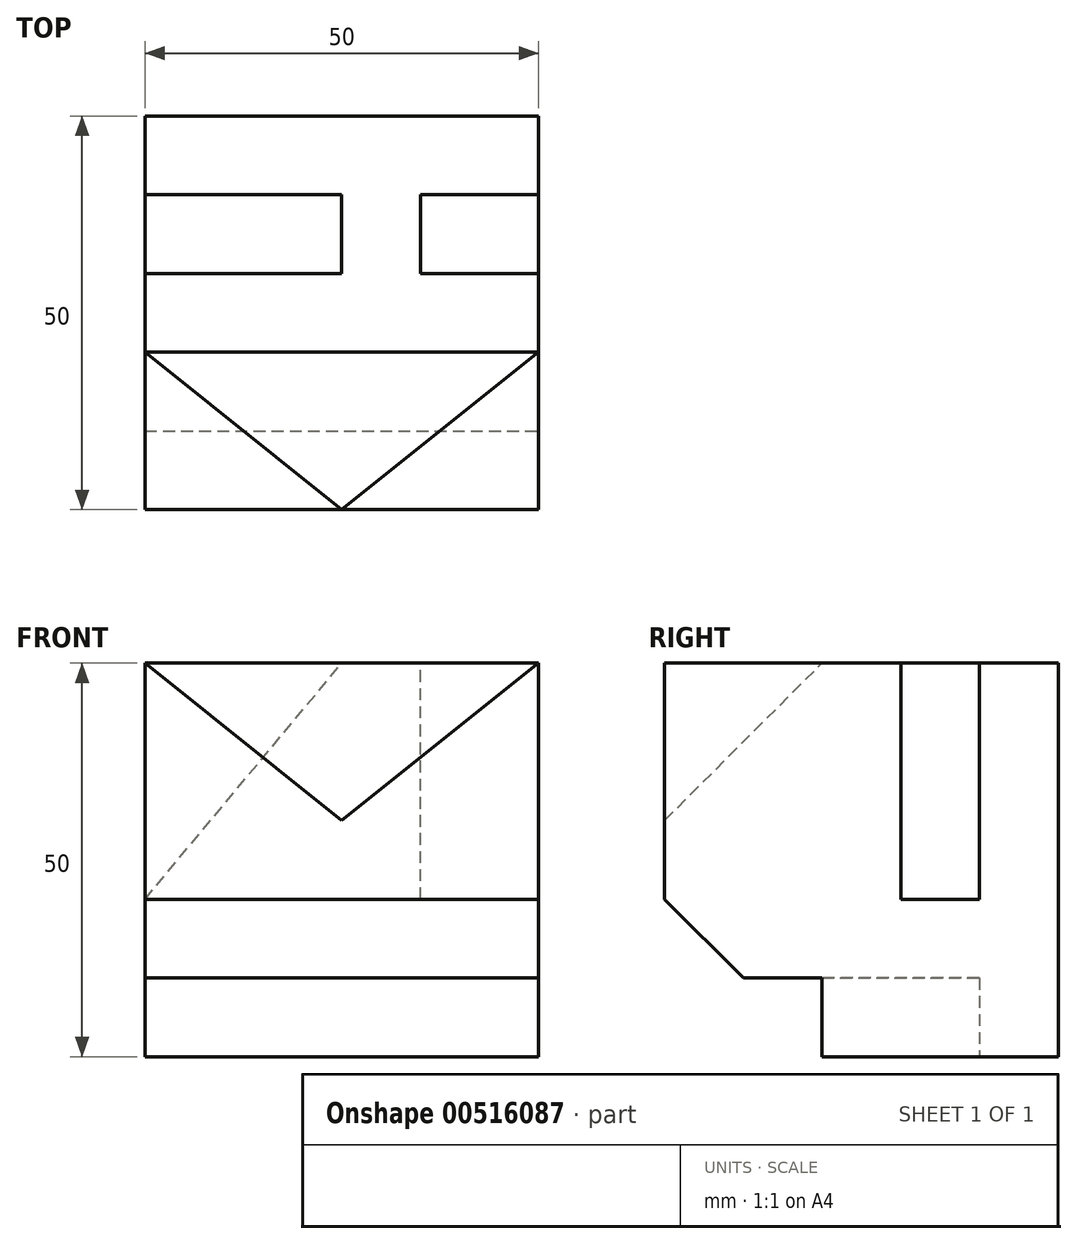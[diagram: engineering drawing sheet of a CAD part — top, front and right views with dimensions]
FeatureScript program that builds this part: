
annotation { "Feature Type Name" : "Feature", "Feature Type Description" : "" }
export const myFeature = defineFeature(function(context is Context, id is Id, definition is map)
    precondition{}
    {
        {
            var Q0;
            Q0=qCreatedBy(makeId("Top.planeOp"),FACE);
            var sketch = newSketch(context, id + "F0", { "sketchPlane" : qUnion([Q0])});
            skLineSegment(sketch, "E0.bottom", {"start": v(0, 0) * mm, "end": v(50, 0) * mm});
            skLineSegment(sketch, "E0.top", {"start": v(0, 50) * mm, "end": v(50, 50) * mm});
            skLineSegment(sketch, "E0.left", {"start": v(0, 0) * mm, "end": v(0, 50) * mm});
            skLineSegment(sketch, "E0.right", {"start": v(50, 0) * mm, "end": v(50, 50) * mm});
            skSolve(sketch);
        }
        {
            var Q0;
            Q0=makeQuery(id+"F0.imprint","IMPRINT",FACE,{"disambiguationData":[TD([[makeQuery(id+"F0.imprint","IMPRINT",EDGE,{"derivedFrom":sQuery(id+"F0.wireOp",EDGE,"E0.bottom")}),1.0]])]});
            extrude(context, id + "F1", {"entities" : qUnion([Q0]), "depth" : 50 * mm, "offsetDistance" : 25 * mm});
        }
        {
            var Q0;
            Q0=makeQuery(id+"F1.opExtrude","SWEPT_FACE",FACE,{"disambiguationData":[OSD([sQuery(id+"F0.wireOp",EDGE,"E0.bottom")])]});
            var sketch = newSketch(context, id + "F2", { "sketchPlane" : qUnion([Q0])});
            skLineSegment(sketch, "E1", {"start": v(0, 50) * mm, "end": v(25, 30) * mm});
            skLineSegment(sketch, "E2", {"start": v(25, 30) * mm, "end": v(50, 50) * mm});
            skSolve(sketch);
        }
        {
            var Q0;
            Q0=makeQuery(id+"F1.opExtrude","SWEPT_FACE",FACE,{"disambiguationData":[OSD([sQuery(id+"F0.wireOp",EDGE,"E0.right")])]});
            var sketch = newSketch(context, id + "F3", { "sketchPlane" : qUnion([Q0])});
            skLineSegment(sketch, "E3", {"start": v(0, 30) * mm, "end": v(20, 50) * mm});
            skSolve(sketch);
        }
        {
            var Q0;
            Q0=makeQuery(id+"F2.imprint","IMPRINT",FACE,{"disambiguationData":[TD([[makeQuery(id+"F2.imprint","IMPRINT",EDGE,{"derivedFrom":sQuery(id+"F2.wireOp",EDGE,"E1")}),1.0]])]});
            var Q1;
            Q1=sQuery(id+"F3.wireOp",EDGE,"E3");
            sweep(context, id + "F4", {"operationType" : NewBodyOperationType.REMOVE, "profiles" : qUnion([Q0]), "path" : qUnion([Q1])});
        }
        {
            var Q0;
            Q0=makeQuery(id+"F1.opExtrude","SWEPT_FACE",FACE,{"disambiguationData":[OSD([sQuery(id+"F0.wireOp",EDGE,"E0.bottom")])]});
            var sketch = newSketch(context, id + "F5", { "sketchPlane" : qUnion([Q0])});
            skLineSegment(sketch, "E4.bottom", {"start": v(0, 0) * mm, "end": v(50, 0) * mm});
            skLineSegment(sketch, "E4.top", {"start": v(0, 10) * mm, "end": v(50, 10) * mm});
            skLineSegment(sketch, "E4.left", {"start": v(0, 0) * mm, "end": v(0, 10) * mm});
            skLineSegment(sketch, "E4.right", {"start": v(50, 0) * mm, "end": v(50, 10) * mm});
            skSolve(sketch);
        }
        {
            var Q0;
            Q0=makeQuery(id+"F5.imprint","IMPRINT",FACE,{"disambiguationData":[TD([[makeQuery(id+"F5.imprint","IMPRINT",EDGE,{"derivedFrom":sQuery(id+"F5.wireOp",EDGE,"E4.bottom")}),1.0]])]});
            extrude(context, id + "F6", {"entities" : qUnion([Q0]), "operationType" : NewBodyOperationType.REMOVE, "oppositeDirection" : true, "depth" : 20 * mm, "offsetDistance" : 25 * mm});
        }
        {
            var Q0;
            Q0=makeQuery(id+"F1.opExtrude","SWEPT_FACE",FACE,{"disambiguationData":[OSD([sQuery(id+"F0.wireOp",EDGE,"E0.right")])]});
            var sketch = newSketch(context, id + "F7", { "sketchPlane" : qUnion([Q0])});
            skLineSegment(sketch, "E5", {"start": v(0, 10) * mm, "end": v(0, 20) * mm});
            skLineSegment(sketch, "E6", {"start": v(0, 10) * mm, "end": v(10, 10) * mm});
            skLineSegment(sketch, "E7", {"start": v(10, 10) * mm, "end": v(0, 20) * mm});
            skSolve(sketch);
        }
        {
            var Q0;
            Q0=makeQuery(id+"F7.imprint","IMPRINT",FACE,{"disambiguationData":[TD([[makeQuery(id+"F7.imprint","IMPRINT",EDGE,{"derivedFrom":sQuery(id+"F7.wireOp",EDGE,"E5")}),1.0]])]});
            extrude(context, id + "F8", {"entities" : qUnion([Q0]), "operationType" : NewBodyOperationType.REMOVE, "endBound" : BoundingType.THROUGH_ALL, "oppositeDirection" : true, "depth" : 25 * mm, "offsetDistance" : 25 * mm});
        }
        {
            var Q0;
            Q0=makeQuery(id+"F1.opExtrude","CAP_FACE",FACE,{"disambiguationData":[OSD([sQuery(id+"F0.wireOp",EDGE,"E0.bottom"),sQuery(id+"F0.wireOp",EDGE,"E0.top"),sQuery(id+"F0.wireOp",EDGE,"E0.left"),sQuery(id+"F0.wireOp",EDGE,"E0.right")])],"isStart":true});
            var sketch = newSketch(context, id + "F9", { "sketchPlane" : qUnion([Q0])});
            skLineSegment(sketch, "E8", {"start": v(50, -20) * mm, "end": v(0, -40) * mm});
            skSolve(sketch);
        }
        {
            var Q0;
            {var subQ0=sQuery(id+"F9.wireOp",EDGE,"E8");Q0=makeQuery(id+"F9.imprint","IMPRINT",FACE,{"disambiguationData":[TD([[makeQuery(id+"F9.imprint","IMPRINT",EDGE,{"derivedFrom":subQ0}),-1.0]])]});}
            extrude(context, id + "F10", {"entities" : qUnion([Q0]), "operationType" : NewBodyOperationType.REMOVE, "oppositeDirection" : true, "depth" : 10 * mm, "offsetDistance" : 25 * mm});
        }
        {
            var Q0;
            Q0=makeQuery(id+"F1.opExtrude","SWEPT_FACE",FACE,{"disambiguationData":[OSD([sQuery(id+"F0.wireOp",EDGE,"E0.left")])]});
            var sketch = newSketch(context, id + "F11", { "sketchPlane" : qUnion([Q0])});
            skLineSegment(sketch, "E9.bottom", {"start": v(-40, 50) * mm, "end": v(-30, 50) * mm});
            skLineSegment(sketch, "E9.top", {"start": v(-40, 20) * mm, "end": v(-30, 20) * mm});
            skLineSegment(sketch, "E9.left", {"start": v(-40, 50) * mm, "end": v(-40, 20) * mm});
            skLineSegment(sketch, "E9.right", {"start": v(-30, 50) * mm, "end": v(-30, 20) * mm});
            skSolve(sketch);
        }
        {
            var Q0;
            Q0=makeQuery(id+"F1.opExtrude","SWEPT_FACE",FACE,{"disambiguationData":[OSD([sQuery(id+"F0.wireOp",EDGE,"E0.top")])]});
            var sketch = newSketch(context, id + "F12", { "sketchPlane" : qUnion([Q0])});
            skLineSegment(sketch, "E10", {"start": v(0, 20) * mm, "end": v(-25, 50) * mm});
            skSolve(sketch);
        }
        {
            var Q0;
            Q0=makeQuery(id+"F11.imprint","IMPRINT",FACE,{"disambiguationData":[TD([[makeQuery(id+"F11.imprint","IMPRINT",EDGE,{"derivedFrom":sQuery(id+"F11.wireOp",EDGE,"E9.bottom")}),1.0]])]});
            var Q1;
            Q1=sQuery(id+"F12.wireOp",EDGE,"E10");
            sweep(context, id + "F13", {"operationType" : NewBodyOperationType.REMOVE, "profiles" : qUnion([Q0]), "path" : qUnion([Q1])});
        }
        {
            var Q0;
            Q0=makeQuery(id+"F1.opExtrude","CAP_FACE",FACE,{"disambiguationData":[OSD([sQuery(id+"F0.wireOp",EDGE,"E0.bottom"),sQuery(id+"F0.wireOp",EDGE,"E0.top"),sQuery(id+"F0.wireOp",EDGE,"E0.left"),sQuery(id+"F0.wireOp",EDGE,"E0.right")])],"isStart":false});
            var sketch = newSketch(context, id + "F14", { "sketchPlane" : qUnion([Q0])});
            skLineSegment(sketch, "E11.bottom", {"start": v(50, 40) * mm, "end": v(35, 40) * mm});
            skLineSegment(sketch, "E11.top", {"start": v(50, 30) * mm, "end": v(35, 30) * mm});
            skLineSegment(sketch, "E11.left", {"start": v(50, 40) * mm, "end": v(50, 30) * mm});
            skLineSegment(sketch, "E11.right", {"start": v(35, 40) * mm, "end": v(35, 30) * mm});
            skSolve(sketch);
        }
        {
            var Q0;
            Q0=makeQuery(id+"F14.imprint","IMPRINT",FACE,{"disambiguationData":[TD([[makeQuery(id+"F14.imprint","IMPRINT",EDGE,{"derivedFrom":sQuery(id+"F14.wireOp",EDGE,"E11.bottom")}),1.0]])]});
            extrude(context, id + "F15", {"entities" : qUnion([Q0]), "operationType" : NewBodyOperationType.REMOVE, "oppositeDirection" : true, "depth" : 30 * mm, "offsetDistance" : 25 * mm});
        }
        {
            var Q0;
            Q0=makeQuery(id+"F1.opExtrude","SWEPT_FACE",FACE,{"disambiguationData":[OSD([sQuery(id+"F0.wireOp",EDGE,"E0.bottom")])]});
            var sketch = newSketch(context, id + "F16", { "sketchPlane" : qUnion([Q0])});
            skLineSegment(sketch, "E12", {"start": v(0, 50) * mm, "end": v(50, 50) * mm});
            skLineSegment(sketch, "E13", {"start": v(50, 50) * mm, "end": v(25, 30) * mm});
            skLineSegment(sketch, "E14", {"start": v(25, 30) * mm, "end": v(0, 50) * mm});
            skSolve(sketch);
        }
        {
            var Q0;
            Q0=makeQuery(id+"F16.imprint","IMPRINT",FACE,{"disambiguationData":[TD([[makeQuery(id+"F16.imprint","IMPRINT",EDGE,{"derivedFrom":sQuery(id+"F16.wireOp",EDGE,"E12")}),-1.0]])]});
            extrude(context, id + "F17", {"entities" : qUnion([Q0]), "operationType" : NewBodyOperationType.REMOVE, "oppositeDirection" : true, "depth" : 20 * mm, "offsetDistance" : 25 * mm});
        }
        {
            var Q0;
            Q0=makeQuery(id+"F17.boolean.opBoolean","COPY",VERTEX,{"derivedFrom":makeQuery(id+"F17.opExtrude","CAP_VERTEX",VERTEX,{"disambiguationData":[OSD([sQuery(id+"F0.wireOp",EDGE,"E0.bottom"),sQuery(id+"F0.wireOp",EDGE,"E0.left"),sQuery(id+"F16.wireOp",EDGE,"E12"),sQuery(id+"F16.wireOp",EDGE,"E14")])],"isStart":false})});
            var Q1;
            Q1=makeQuery(id+"F17.boolean.opBoolean","COPY",VERTEX,{"derivedFrom":makeQuery(id+"F17.opExtrude","CAP_VERTEX",VERTEX,{"disambiguationData":[OSD([sQuery(id+"F0.wireOp",EDGE,"E0.bottom"),sQuery(id+"F0.wireOp",EDGE,"E0.right"),sQuery(id+"F16.wireOp",EDGE,"E12"),sQuery(id+"F16.wireOp",EDGE,"E13")])],"isStart":false})});
            var Q2;
            Q2=sQuery(id+"F16.wireOp",VERTEX,"E14.start");
            cPlane(context, id + "F18", {"entities" : qUnion([Q0, Q1, Q2]), "cplaneType" : CPlaneType.THREE_POINT, "offset" : 25 * mm, "width" : 150 * mm, "height" : 150 * mm});
        }
        {
            var Q0;
            Q0=makeQuery(id+"F17.boolean.opBoolean","COPY",FACE,{"derivedFrom":makeQuery(id+"F17.opExtrude","CAP_FACE",FACE,{"disambiguationData":[OSD([sQuery(id+"F16.wireOp",EDGE,"E12"),sQuery(id+"F16.wireOp",EDGE,"E13"),sQuery(id+"F16.wireOp",EDGE,"E14")])],"isStart":false})});
            var Q1;
            Q1=qCreatedBy(id+"F18.planeOp",FACE);
            extrude(context, id + "F19", {"entities" : qUnion([Q0]), "operationType" : NewBodyOperationType.ADD, "endBound" : BoundingType.UP_TO_SURFACE, "depth" : 25 * mm, "endBoundEntityFace" : qUnion([Q1]), "offsetDistance" : 25 * mm});
        }
    });
